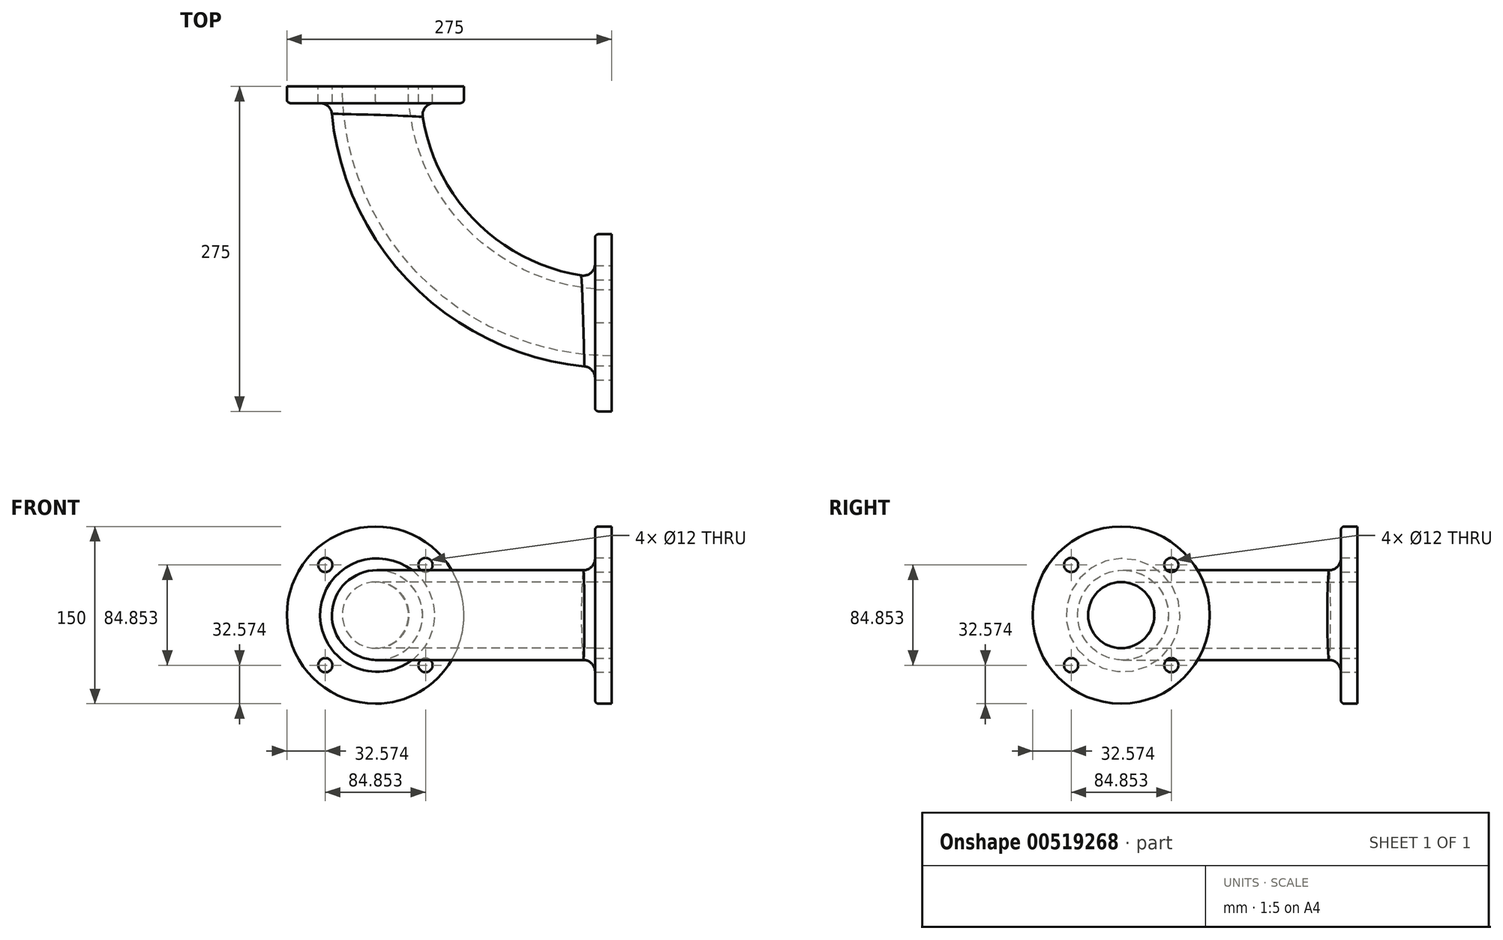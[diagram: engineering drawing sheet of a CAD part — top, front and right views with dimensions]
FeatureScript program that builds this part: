
annotation { "Feature Type Name" : "Feature", "Feature Type Description" : "" }
export const myFeature = defineFeature(function(context is Context, id is Id, definition is map)
    precondition{}
    {
        {
            var Q0;
            Q0=qCreatedBy(makeId("Top.planeOp"),FACE);
            var sketch = newSketch(context, id + "F0", { "sketchPlane" : qUnion([Q0])});
            skArc(sketch, "E0", {"start": v(-200, 0) * mm, "mid": v(-141.42, -141.42) * mm, "end": v(0, -200) * mm});
            skLineSegment(sketch, "E1", {"start": v(-200, 0) * mm, "end": v(0, 0) * mm, "construction": true});
            skLineSegment(sketch, "E2", {"start": v(0, -200) * mm, "end": v(0, 0) * mm, "construction": true});
            skSolve(sketch);
        }
        {
            var Q0;
            Q0=qCreatedBy(makeId("Front.planeOp"),FACE);
            var sketch = newSketch(context, id + "F1", { "sketchPlane" : qUnion([Q0])});
            skCircle(sketch, "E3", {"center": v(-200, 0) * mm, "radius": 28 * mm});
            skCircle(sketch, "E4", {"center": v(-200, 0) * mm, "radius": 38 * mm});
            skSolve(sketch);
        }
        {
            var Q0;
            Q0=qCreatedBy(makeId("Front.planeOp"),FACE);
            var sketch = newSketch(context, id + "F2", { "sketchPlane" : qUnion([Q0])});
            skCircle(sketch, "E5", {"center": v(-200, 0) * mm, "radius": 75 * mm});
            skCircle(sketch, "E6.0", {"center": v(-200, 0) * mm, "radius": 28 * mm});
            skCircle(sketch, "E7", {"center": v(-200, 0) * mm, "radius": 60 * mm, "construction": true});
            skCircle(sketch, "E8", {"center": v(-242.43, 42.43) * mm, "radius": 6 * mm});
            skCircle(sketch, "E9", {"center": v(-157.57, 42.43) * mm, "radius": 6 * mm});
            skCircle(sketch, "E10", {"center": v(-157.57, -42.43) * mm, "radius": 6 * mm});
            skCircle(sketch, "E11", {"center": v(-242.43, -42.43) * mm, "radius": 6 * mm});
            skLineSegment(sketch, "E12", {"start": v(-242.43, -42.43) * mm, "end": v(-157.57, 42.43) * mm, "construction": true});
            skLineSegment(sketch, "E13", {"start": v(-242.43, 42.43) * mm, "end": v(-157.57, -42.43) * mm, "construction": true});
            skLineSegment(sketch, "E14", {"start": v(-200, 0) * mm, "end": v(-280.27, 0) * mm, "construction": true});
            skSolve(sketch);
        }
        {
            var Q0;
            Q0=makeQuery(id+"F1.imprint","IMPRINT",FACE,{"disambiguationData":[TD([[makeQuery(id+"F1.imprint","IMPRINT",EDGE,{"derivedFrom":sQuery(id+"F1.wireOp",EDGE,"E3")}),-1.0]])]});
            var Q1;
            Q1=sQuery(id+"F0.wireOp",EDGE,"E0");
            sweep(context, id + "F3", {"profiles" : qUnion([Q0]), "path" : qUnion([Q1])});
        }
        {
            var Q0;
            Q0=makeQuery(id+"F2.imprint","IMPRINT",FACE,{"disambiguationData":[TD([[makeQuery(id+"F2.imprint","IMPRINT",EDGE,{"derivedFrom":sQuery(id+"F2.wireOp",EDGE,"E5")}),1.0]])]});
            extrude(context, id + "F4", {"entities" : qUnion([Q0]), "depth" : 14 * mm, "offsetDistance" : 25 * mm});
        }
        {
            var Q0;
            Q0=makeQuery(id+"F3.opSweep","CAP_FACE",FACE,{"disambiguationData":[OSD([sQuery(id+"F0.wireOp",VERTEX,"E0.end"),sQuery(id+"F1.wireOp",EDGE,"E3"),sQuery(id+"F1.wireOp",EDGE,"E4")])],"isStart":false});
            var Q1;
            Q1=makeQuery(id+"F3.opSweep","CAP_FACE",FACE,{"disambiguationData":[OSD([sQuery(id+"F0.wireOp",VERTEX,"E0.start"),sQuery(id+"F1.wireOp",EDGE,"E3"),sQuery(id+"F1.wireOp",EDGE,"E4")])],"isStart":true});
            cPlane(context, id + "F5", {"entities" : qUnion([Q0, Q1]), "cplaneType" : CPlaneType.MID_PLANE, "offset" : 25 * mm, "width" : 150 * mm, "height" : 150 * mm});
        }
        {
            var Q0;
            Q0=makeQuery(id+"F4.opExtrude","SWEPT_BODY",BODY,{"disambiguationData":[OSD([sQuery(id+"F2.wireOp",EDGE,"E5"),sQuery(id+"F2.wireOp",EDGE,"E6.0"),sQuery(id+"F2.wireOp",EDGE,"E8"),sQuery(id+"F2.wireOp",EDGE,"E9"),sQuery(id+"F2.wireOp",EDGE,"E10"),sQuery(id+"F2.wireOp",EDGE,"E11")])]});
            var Q1;
            Q1=qCreatedBy(id+"F5.planeOp",FACE);
            mirror(context, id + "F6", {"operationType" : NewBodyOperationType.ADD, "entities" : qUnion([Q0]), "mirrorPlane" : qUnion([Q1])});
        }
        {
            var Q0;
            Q0=makeQuery(id+"F4.opExtrude","CAP_EDGE",EDGE,{"disambiguationData":[OSD([sQuery(id+"F2.wireOp",EDGE,"E5")])],"isStart":false});
            var Q1;
            Q1=makeQuery(id+"F6.opPattern","COPY",EDGE,{"derivedFrom":makeQuery(id+"F4.opExtrude","CAP_EDGE",EDGE,{"disambiguationData":[OSD([sQuery(id+"F2.wireOp",EDGE,"E5")])],"isStart":false}),"instanceName":"1"});
            fillet(context, id + "F7", {"entities" : qUnion([Q0, Q1]), "radius" : 3 * mm, "tangentPropagation" : true, "allowEdgeOverflow" : false});
        }
        {
            var Q0;
            Q0=makeQuery(id+"F6.boolean.opBoolean","INTERSECT",EDGE,{"derivedFrom":[makeQuery(id+"F3.opSweep","SWEPT_FACE",FACE,{"disambiguationData":[OSD([sQuery(id+"F0.wireOp",EDGE,"E0"),sQuery(id+"F1.wireOp",EDGE,"E4")])]}),makeQuery(id+"F4.opExtrude","CAP_FACE",FACE,{"disambiguationData":[OSD([sQuery(id+"F2.wireOp",EDGE,"E5"),sQuery(id+"F2.wireOp",EDGE,"E6.0"),sQuery(id+"F2.wireOp",EDGE,"E8"),sQuery(id+"F2.wireOp",EDGE,"E9"),sQuery(id+"F2.wireOp",EDGE,"E10"),sQuery(id+"F2.wireOp",EDGE,"E11")])],"isStart":false})]});
            var Q1;
            Q1=makeQuery(id+"F6.boolean.opBoolean","INTERSECT",EDGE,{"derivedFrom":[makeQuery(id+"F3.opSweep","SWEPT_FACE",FACE,{"disambiguationData":[OSD([sQuery(id+"F0.wireOp",EDGE,"E0"),sQuery(id+"F1.wireOp",EDGE,"E4")])]}),makeQuery(id+"F6.opPattern","COPY",FACE,{"derivedFrom":makeQuery(id+"F4.opExtrude","CAP_FACE",FACE,{"disambiguationData":[OSD([sQuery(id+"F2.wireOp",EDGE,"E5"),sQuery(id+"F2.wireOp",EDGE,"E6.0"),sQuery(id+"F2.wireOp",EDGE,"E8"),sQuery(id+"F2.wireOp",EDGE,"E9"),sQuery(id+"F2.wireOp",EDGE,"E10"),sQuery(id+"F2.wireOp",EDGE,"E11")])],"isStart":false}),"instanceName":"1"})]});
            fillet(context, id + "F8", {"entities" : qUnion([Q0, Q1]), "radius" : 10 * mm, "tangentPropagation" : true, "allowEdgeOverflow" : false});
        }
    });
